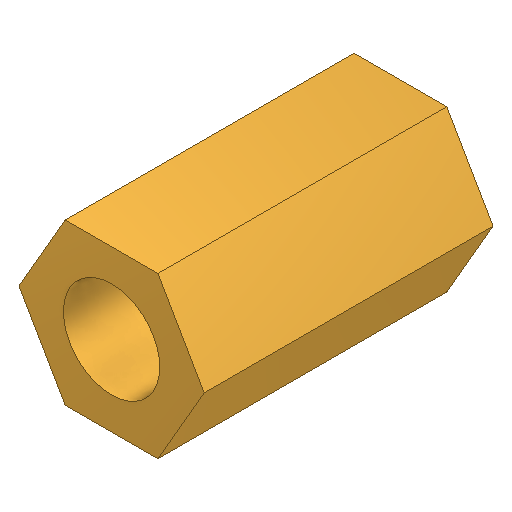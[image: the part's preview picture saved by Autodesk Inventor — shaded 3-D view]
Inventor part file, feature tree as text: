
AUTODESK INVENTOR PART (.ipt)
format: ipt  version: 2025.2 (Build 292293000, 293)  size: 111,616 bytes
history: native  units: mm
features: extrude x1, sketch x1
ambient origin geometry x8: Origin, YZ Plane, XZ Plane, XY Plane, X Axis, Y Axis, Z Axis, Center Point
bodies: Solid1 (feature_tree)
feature tree (2):
  extrude  "Extrusion1"  Depth=9.0mm
  sketch  "Sketch1"  dims[d0=5.0mm d1=3.0mm d2=9.0mm d3=0.0mm]
